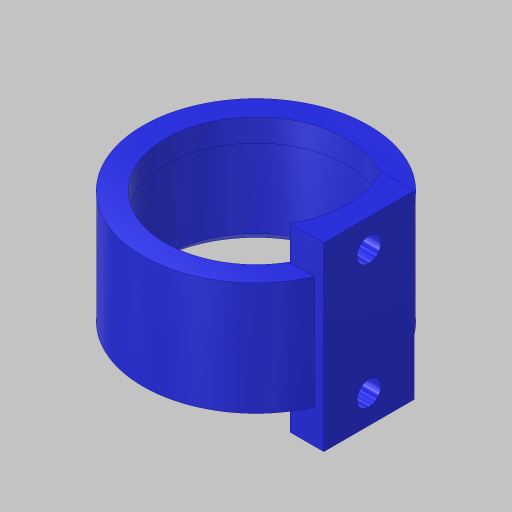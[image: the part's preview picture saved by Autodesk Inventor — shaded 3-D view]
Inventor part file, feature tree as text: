
AUTODESK INVENTOR PART (.ipt)
format: ipt  version: 2023.5 (Build 275446000, 446)  size: 188,928 bytes
history: native  units: in
note: dims shown in document units (in); Inventor stores cm internally (conversion verified against a paired STEP export)
features: extrude x4, sketch x3, chamfer x2, plane x1, mirror x1, projected_geometry x1
ambient origin geometry x8: Origin, YZ Plane, XZ Plane, XY Plane, X Axis, Y Axis, Z Axis, Center Point
bodies: Solid1 (feature_tree)
feature tree (12):
  extrude  "Extrusion1"  Depth=2.5in
  extrude  "Extrusion2"  Depth=2.02in
  chamfer  "Chamfer1"  Distance=1.0in
  plane  "Work Plane1"
  sketch  "Sketch5"  dims[d21=0.125in d22=0.125in d23=45.0deg d27=2.5in d28=2.0in d29=0.2638in d30=0.25in d31=0.0in d32=0.0312in d33=0.125in d34=45.0deg d35=1.0in d36=1.375in d37=2.0in d38=1.0in d39=0.0in]
  extrude  "Extrusion4"  Depth=2.5in
  extrude  "Extrusion5"  Depth=2.0in
  mirror  "Mirror1"
  chamfer  "Chamfer3"  Distance=0.2638in
  sketch  "Sketch1"  dims[d0=2.0in d1=2.5in]
  sketch  "Sketch2"  dims[d2=0.25in d3=0.0in d4=2.02in d5=1.0in d6=0.0in]
  projected_geometry  "Projected Loop1"
